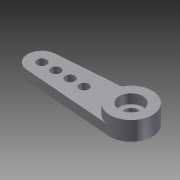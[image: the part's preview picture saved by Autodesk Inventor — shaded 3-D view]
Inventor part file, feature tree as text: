
AUTODESK INVENTOR PART (.ipt)
format: ipt  version: 2012 (Build 160160000, 160)  size: 119,808 bytes
history: native  units: mm
features: sketch x4, extrude x2, hole x2
ambient origin geometry x8: Origin, YZ Plane, XZ Plane, XY Plane, X Axis, Y Axis, Z Axis, Center Point
bodies: Solid1 (feature_tree)
feature tree (8):
  extrude  "Extrusion1"  Depth=2.0mm TaperAngle=0.0deg
  extrude  "Extrusion2"  Depth=2.0mm TaperAngle=0.0deg
  hole  "Hole1"  [1 undecoded]
  hole  "Hole2"  [1 undecoded]
  sketch  "Sketch1"  dims[d1=2.0mm d2=2.0mm d3=3.0mm d6=3.0mm d8=6.0mm d9=9.0mm d10=3.0mm d11=2.0mm d12=0.0mm]
  sketch  "Sketch2"  dims[d13=9.0mm d14=2.0mm d15=0.0mm]
  sketch  "Sketch3"  dims[d16=5.0mm]
  sketch  "Sketch4"  dims[d17=5.0mm d18=6.0mm d19=4.0mm d20=2.0mm d21=90.0deg d22=2.0mm d23=0.0mm d24=2.0mm d25=2.0mm d26=3.0mm d27=3.0mm d28=2.0mm d29=6.0mm d30=4.0mm d31=2.0mm d32=90.0deg d33=2.0mm d34=0.0mm]
note: 2 required parameter values undecoded (feature->parameter linkage not recoverable at this tier; creation-order binding heuristic only, values carry confidence <= 0.55)
